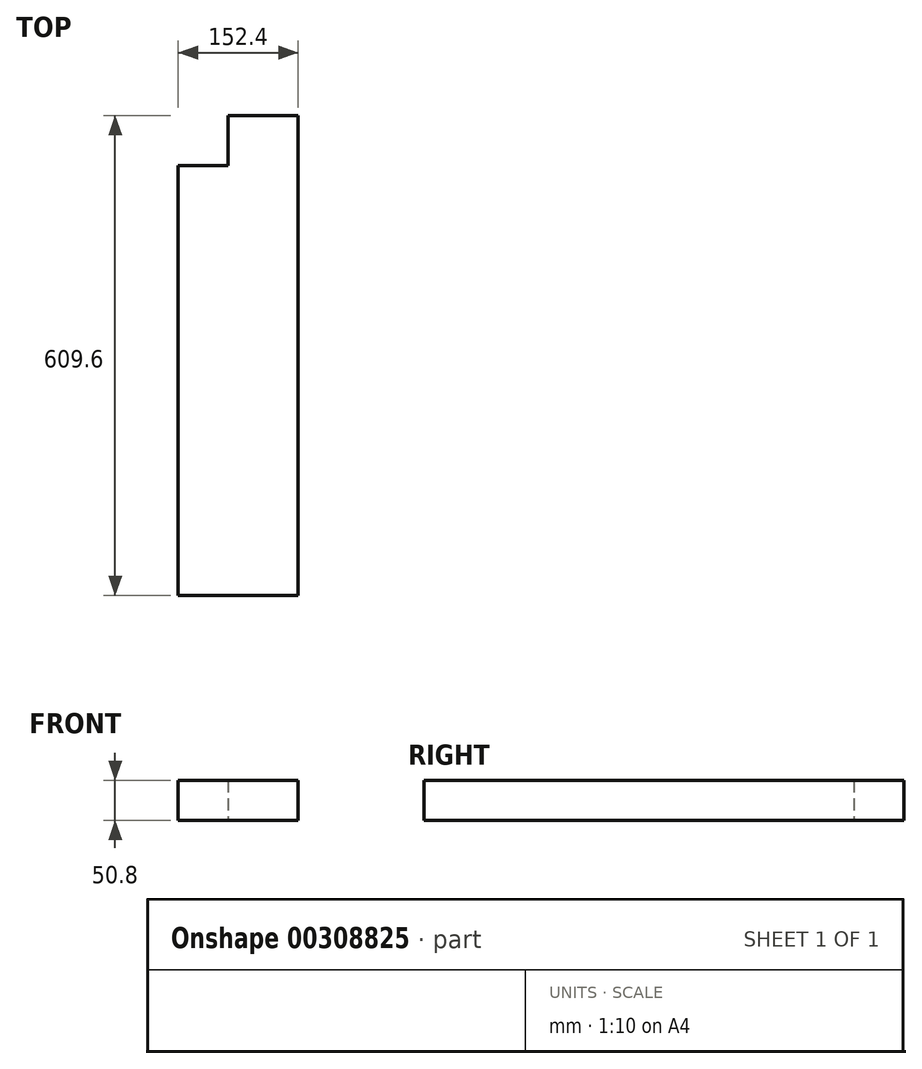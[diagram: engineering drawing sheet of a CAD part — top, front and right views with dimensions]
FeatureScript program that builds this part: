
annotation { "Feature Type Name" : "Feature", "Feature Type Description" : "" }
export const myFeature = defineFeature(function(context is Context, id is Id, definition is map)
    precondition{}
    {
        {
            var Q0;
            Q0=qCreatedBy(makeId("Top.planeOp"),FACE);
            var sketch = newSketch(context, id + "F0", { "sketchPlane" : qUnion([Q0])});
            skLineSegment(sketch, "E0.bottom", {"start": v(63.5, 0) * mm, "end": v(152.4, 0) * mm});
            skLineSegment(sketch, "E0.top", {"start": v(0, -609.6) * mm, "end": v(152.4, -609.6) * mm});
            skLineSegment(sketch, "E0.left", {"start": v(0, -63.5) * mm, "end": v(0, -609.6) * mm});
            skLineSegment(sketch, "E0.right", {"start": v(152.4, 0) * mm, "end": v(152.4, -609.6) * mm});
            skLineSegment(sketch, "E1", {"start": v(0, -63.5) * mm, "end": v(63.5, -63.5) * mm});
            skLineSegment(sketch, "E2", {"start": v(63.5, -63.5) * mm, "end": v(63.5, 0) * mm});
            skSolve(sketch);
        }
        {
            var Q0;
            Q0 = qSketchRegion(id + "F0", true);
            extrude(context, id + "F1", {"entities" : qUnion([Q0]), "depth" : 50.8 * mm});
        }
    });
